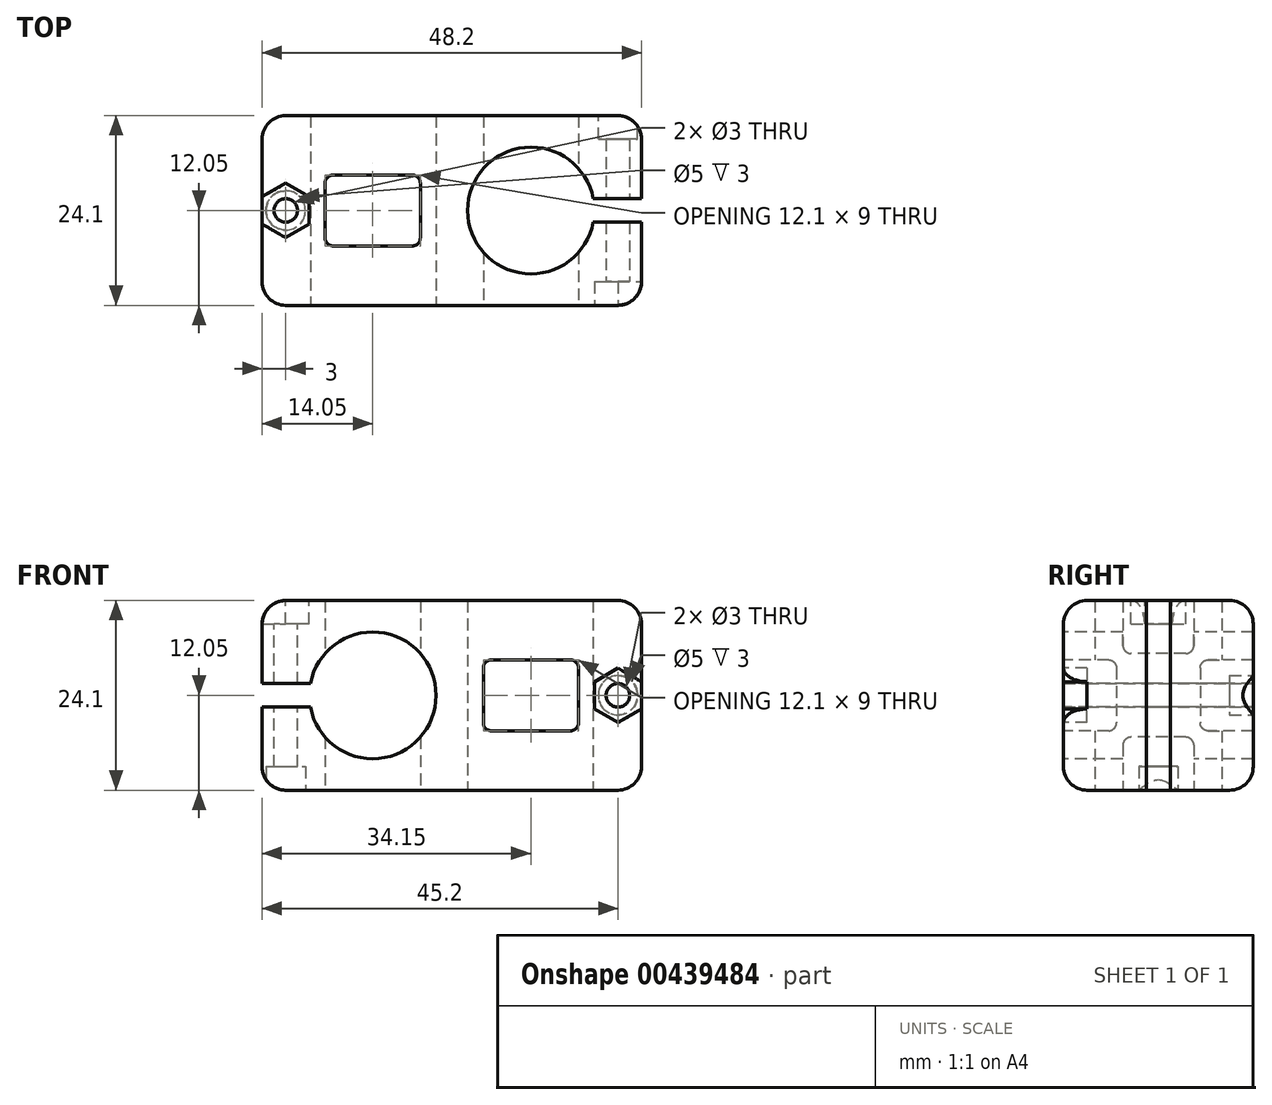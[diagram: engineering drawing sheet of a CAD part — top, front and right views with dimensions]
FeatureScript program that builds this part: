
annotation { "Feature Type Name" : "Feature", "Feature Type Description" : "" }
export const myFeature = defineFeature(function(context is Context, id is Id, definition is map)
    precondition{}
    {
        {
            var Q0;
            Q0=qCreatedBy(makeId("Top.planeOp"),FACE);
            var sketch = newSketch(context, id + "F0", { "sketchPlane" : qUnion([Q0])});
            skLineSegment(sketch, "E0", {"start": v(-10.05, 0) * mm, "end": v(10.05, 0) * mm, "construction": true});
            skCircle(sketch, "E1", {"center": v(10.05, 0) * mm, "radius": 8.05 * mm});
            skLineSegment(sketch, "E2.bottom", {"start": v(-24.1, 12.05) * mm, "end": v(24.1, 12.05) * mm});
            skLineSegment(sketch, "E2.top", {"start": v(-24.1, -12.05) * mm, "end": v(24.1, -12.05) * mm});
            skLineSegment(sketch, "E2.left", {"start": v(-24.1, 12.05) * mm, "end": v(-24.1, -12.05) * mm});
            skLineSegment(sketch, "E2.right", {"start": v(24.1, 12.05) * mm, "end": v(24.1, -12.05) * mm});
            skLineSegment(sketch, "E3.bottom", {"start": v(-16.1, 4.5) * mm, "end": v(-4, 4.5) * mm});
            skLineSegment(sketch, "E3.top", {"start": v(-16.1, -4.5) * mm, "end": v(-4, -4.5) * mm});
            skLineSegment(sketch, "E3.left", {"start": v(-16.1, 4.5) * mm, "end": v(-16.1, -4.5) * mm});
            skLineSegment(sketch, "E3.right", {"start": v(-4, 4.5) * mm, "end": v(-4, -4.5) * mm});
            skPoint(sketch, "E3.middle", {"position": v(-10.05, 0) * mm});
            skSolve(sketch);
        }
        {
            var Q0;
            Q0 = qSketchRegion(id + "F0", true);
            extrude(context, id + "F1", {"entities" : qUnion([Q0]), "endBound" : BoundingType.SYMMETRIC, "depth" : 24.1 * mm});
        }
        {
            var Q0;
            Q0=makeQuery(id+"F1.opExtrude","SWEPT_FACE",FACE,{"disambiguationData":[OSD([sQuery(id+"F0.wireOp",EDGE,"E2.top")])]});
            var sketch = newSketch(context, id + "F2", { "sketchPlane" : qUnion([Q0])});
            skLineSegment(sketch, "E4", {"start": v(10.05, 0) * mm, "end": v(-10.05, 0) * mm, "construction": true});
            skPoint(sketch, "E4.startSnap0", {"position": v(24.1, 0) * mm});
            skPoint(sketch, "E4.endSnap0", {"position": v(24.1, 0) * mm});
            skCircle(sketch, "E5", {"center": v(-10.05, 0) * mm, "radius": 8.05 * mm});
            skLineSegment(sketch, "E6.bottom", {"start": v(16.1, 4.5) * mm, "end": v(4, 4.5) * mm});
            skLineSegment(sketch, "E6.top", {"start": v(16.1, -4.5) * mm, "end": v(4, -4.5) * mm});
            skLineSegment(sketch, "E6.left", {"start": v(16.1, 4.5) * mm, "end": v(16.1, -4.5) * mm});
            skLineSegment(sketch, "E6.right", {"start": v(4, 4.5) * mm, "end": v(4, -4.5) * mm});
            skPoint(sketch, "E6.middle", {"position": v(10.05, 0) * mm});
            skSolve(sketch);
        }
        {
            var Q0;
            Q0 = qSketchRegion(id + "F2", true);
            extrude(context, id + "F3", {"entities" : qUnion([Q0]), "operationType" : NewBodyOperationType.REMOVE, "oppositeDirection" : true, "depth" : 25 * mm});
        }
        {
            var Q0;
            Q0=makeQuery(id+"F1.opExtrude","SWEPT_FACE",FACE,{"disambiguationData":[OSD([sQuery(id+"F0.wireOp",EDGE,"E2.bottom")])]});
            var sketch = newSketch(context, id + "F4", { "sketchPlane" : qUnion([Q0])});
            skLineSegment(sketch, "E7.bottom", {"start": v(16.26, -1.5) * mm, "end": v(36.47, -1.5) * mm});
            skLineSegment(sketch, "E7.top", {"start": v(16.26, 1.5) * mm, "end": v(36.47, 1.5) * mm});
            skLineSegment(sketch, "E7.left", {"start": v(16.26, -1.5) * mm, "end": v(16.26, 1.5) * mm});
            skLineSegment(sketch, "E7.right", {"start": v(36.47, -1.5) * mm, "end": v(36.47, 1.5) * mm});
            skPoint(sketch, "E7.middle", {"position": v(26.36, 0) * mm});
            skPoint(sketch, "E7.middle.positionSnap0", {"position": v(24.1, 0) * mm});
            skPoint(sketch, "E7.centerSnap0", {"position": v(24.1, 0) * mm});
            skSolve(sketch);
        }
        {
            var Q0;
            Q0 = qSketchRegion(id + "F4", true);
            extrude(context, id + "F5", {"entities" : qUnion([Q0]), "operationType" : NewBodyOperationType.REMOVE, "oppositeDirection" : true, "depth" : 25 * mm});
        }
        {
            var Q0;
            Q0=makeQuery(id+"F1.opExtrude","CAP_FACE",FACE,{"disambiguationData":[OSD([sQuery(id+"F0.wireOp",EDGE,"E1"),sQuery(id+"F0.wireOp",EDGE,"E2.bottom"),sQuery(id+"F0.wireOp",EDGE,"E2.top"),sQuery(id+"F0.wireOp",EDGE,"E2.left"),sQuery(id+"F0.wireOp",EDGE,"E2.right"),sQuery(id+"F0.wireOp",EDGE,"E3.bottom"),sQuery(id+"F0.wireOp",EDGE,"E3.top"),sQuery(id+"F0.wireOp",EDGE,"E3.left"),sQuery(id+"F0.wireOp",EDGE,"E3.right")])],"isStart":true});
            var sketch = newSketch(context, id + "F6", { "sketchPlane" : qUnion([Q0])});
            skLineSegment(sketch, "E8.bottom", {"start": v(16.57, 1.5) * mm, "end": v(31.63, 1.5) * mm});
            skLineSegment(sketch, "E8.top", {"start": v(16.57, -1.5) * mm, "end": v(31.63, -1.5) * mm});
            skLineSegment(sketch, "E8.left", {"start": v(16.57, 1.5) * mm, "end": v(16.57, -1.5) * mm});
            skLineSegment(sketch, "E8.right", {"start": v(31.63, 1.5) * mm, "end": v(31.63, -1.5) * mm});
            skPoint(sketch, "E8.middle", {"position": v(24.1, 0) * mm});
            skSolve(sketch);
        }
        {
            var Q0;
            Q0 = qSketchRegion(id + "F6", true);
            extrude(context, id + "F7", {"entities" : qUnion([Q0]), "operationType" : NewBodyOperationType.REMOVE, "endBound" : BoundingType.THROUGH_ALL, "oppositeDirection" : true, "depth" : 25 * mm});
        }
        {
            var Q0;
            Q0=makeQuery(id+"F1.opExtrude","SWEPT_FACE",FACE,{"disambiguationData":[OSD([sQuery(id+"F0.wireOp",EDGE,"E2.top")])]});
            var sketch = newSketch(context, id + "F8", { "sketchPlane" : qUnion([Q0])});
            skCircle(sketch, "E9.cCircle", {"center": v(21.1, 0) * mm, "radius": 3 * mm, "construction": true});
            skLineSegment(sketch, "E9.0", {"start": v(18.1, 1.73) * mm, "end": v(21.1, 3.46) * mm});
            skLineSegment(sketch, "E9.1", {"start": v(21.1, 3.46) * mm, "end": v(24.1, 1.73) * mm});
            skLineSegment(sketch, "E9.2", {"start": v(24.1, 1.73) * mm, "end": v(24.1, -1.73) * mm});
            skLineSegment(sketch, "E9.3", {"start": v(24.1, -1.73) * mm, "end": v(21.1, -3.46) * mm});
            skLineSegment(sketch, "E9.4", {"start": v(21.1, -3.46) * mm, "end": v(18.1, -1.73) * mm});
            skLineSegment(sketch, "E9.5", {"start": v(18.1, -1.73) * mm, "end": v(18.1, 1.73) * mm});
            skPoint(sketch, "E9.0.midPoint", {"position": v(19.6, 2.6) * mm});
            skSolve(sketch);
        }
        {
            var Q0;
            Q0 = qSketchRegion(id + "F8", true);
            extrude(context, id + "F9", {"entities" : qUnion([Q0]), "operationType" : NewBodyOperationType.REMOVE, "oppositeDirection" : true, "depth" : 3 * mm});
        }
        {
            var Q0;
            Q0=makeQuery(id+"F9.boolean.opBoolean","COPY",FACE,{"derivedFrom":makeQuery(id+"F9.opExtrude","CAP_FACE",FACE,{"disambiguationData":[OSD([sQuery(id+"F8.wireOp",EDGE,"E9.0"),sQuery(id+"F8.wireOp",EDGE,"E9.1"),sQuery(id+"F8.wireOp",EDGE,"E9.2"),sQuery(id+"F8.wireOp",EDGE,"E9.3"),sQuery(id+"F8.wireOp",EDGE,"E9.4"),sQuery(id+"F8.wireOp",EDGE,"E9.5")])],"isStart":false})});
            var sketch = newSketch(context, id + "F10", { "sketchPlane" : qUnion([Q0])});
            skLineSegment(sketch, "E10", {"start": v(21.1, 3.46) * mm, "end": v(21.1, -3.46) * mm, "construction": true});
            skCircle(sketch, "E11", {"center": v(21.1, 0) * mm, "radius": 1.5 * mm});
            skSolve(sketch);
        }
        {
            var Q0;
            Q0=makeQuery(id+"F10.imprint","IMPRINT",FACE,{"disambiguationData":[TD([[makeQuery(id+"F10.imprint","IMPRINT",EDGE,{"derivedFrom":sQuery(id+"F10.wireOp",EDGE,"E11")}),1.0]])]});
            extrude(context, id + "F11", {"entities" : qUnion([Q0]), "operationType" : NewBodyOperationType.REMOVE, "endBound" : BoundingType.THROUGH_ALL, "oppositeDirection" : true, "depth" : 25 * mm});
        }
        {
            var Q0;
            Q0=makeQuery(id+"F1.opExtrude","SWEPT_FACE",FACE,{"disambiguationData":[OSD([sQuery(id+"F0.wireOp",EDGE,"E2.bottom")])]});
            var sketch = newSketch(context, id + "F12", { "sketchPlane" : qUnion([Q0])});
            skCircle(sketch, "E12", {"center": v(-21.1, 0) * mm, "radius": 2.5 * mm});
            skSolve(sketch);
        }
        {
            var Q0;
            Q0 = qSketchRegion(id + "F12", true);
            extrude(context, id + "F13", {"entities" : qUnion([Q0]), "operationType" : NewBodyOperationType.REMOVE, "oppositeDirection" : true, "depth" : 3 * mm});
        }
        {
            var Q0;
            {var subQ0=sQuery(id+"F2.wireOp",EDGE,"E6.left");var subQ1=sQuery(id+"F2.wireOp",EDGE,"E6.bottom");Q0=makeQuery(id+"F3.boolean.opBoolean","COPY",EDGE,{"disambiguationData":[TD([makeQuery(id+"F1.opExtrude","SWEPT_FACE",FACE,{"disambiguationData":[OSD([sQuery(id+"F0.wireOp",EDGE,"E2.top")])]})])],"derivedFrom":makeQuery(id+"F3.opExtrude","SWEPT_EDGE",EDGE,{"disambiguationData":[OSD([subQ1,subQ0])]})});}
            var Q1;
            {var subQ0=sQuery(id+"F2.wireOp",EDGE,"E6.left");var subQ1=sQuery(id+"F2.wireOp",EDGE,"E6.top");Q1=makeQuery(id+"F3.boolean.opBoolean","COPY",EDGE,{"disambiguationData":[TD([makeQuery(id+"F1.opExtrude","SWEPT_FACE",FACE,{"disambiguationData":[OSD([sQuery(id+"F0.wireOp",EDGE,"E2.top")])]})])],"derivedFrom":makeQuery(id+"F3.opExtrude","SWEPT_EDGE",EDGE,{"disambiguationData":[OSD([subQ1,subQ0])]})});}
            var Q2;
            {var subQ0=sQuery(id+"F2.wireOp",EDGE,"E6.bottom");var subQ1=sQuery(id+"F2.wireOp",EDGE,"E6.right");Q2=makeQuery(id+"F3.boolean.opBoolean","COPY",EDGE,{"disambiguationData":[TD([makeQuery(id+"F1.opExtrude","SWEPT_FACE",FACE,{"disambiguationData":[OSD([sQuery(id+"F0.wireOp",EDGE,"E2.top")])]})])],"derivedFrom":makeQuery(id+"F3.opExtrude","SWEPT_EDGE",EDGE,{"disambiguationData":[OSD([subQ0,subQ1])]})});}
            var Q3;
            {var subQ0=sQuery(id+"F2.wireOp",EDGE,"E6.top");var subQ1=sQuery(id+"F2.wireOp",EDGE,"E6.right");Q3=makeQuery(id+"F3.boolean.opBoolean","COPY",EDGE,{"disambiguationData":[TD([makeQuery(id+"F1.opExtrude","SWEPT_FACE",FACE,{"disambiguationData":[OSD([sQuery(id+"F0.wireOp",EDGE,"E2.top")])]})])],"derivedFrom":makeQuery(id+"F3.opExtrude","SWEPT_EDGE",EDGE,{"disambiguationData":[OSD([subQ0,subQ1])]})});}
            var Q4;
            {var subQ0=sQuery(id+"F0.wireOp",EDGE,"E3.right");var subQ1=sQuery(id+"F0.wireOp",EDGE,"E3.top");Q4=makeQuery(id+"F3.boolean.opBoolean","SPLIT",EDGE,{"disambiguationData":[TD([makeQuery(id+"F1.opExtrude","CAP_FACE",FACE,{"disambiguationData":[OSD([sQuery(id+"F0.wireOp",EDGE,"E1"),sQuery(id+"F0.wireOp",EDGE,"E2.bottom"),sQuery(id+"F0.wireOp",EDGE,"E2.top"),sQuery(id+"F0.wireOp",EDGE,"E2.left"),sQuery(id+"F0.wireOp",EDGE,"E2.right"),sQuery(id+"F0.wireOp",EDGE,"E3.bottom"),subQ1,sQuery(id+"F0.wireOp",EDGE,"E3.left"),subQ0])],"isStart":false})])],"derivedFrom":makeQuery(id+"F1.opExtrude","SWEPT_EDGE",EDGE,{"disambiguationData":[OSD([subQ1,subQ0])]})});}
            var Q5;
            {var subQ0=sQuery(id+"F0.wireOp",EDGE,"E3.right");var subQ1=sQuery(id+"F0.wireOp",EDGE,"E3.bottom");Q5=makeQuery(id+"F3.boolean.opBoolean","SPLIT",EDGE,{"disambiguationData":[TD([makeQuery(id+"F1.opExtrude","CAP_FACE",FACE,{"disambiguationData":[OSD([sQuery(id+"F0.wireOp",EDGE,"E1"),sQuery(id+"F0.wireOp",EDGE,"E2.bottom"),sQuery(id+"F0.wireOp",EDGE,"E2.top"),sQuery(id+"F0.wireOp",EDGE,"E2.left"),sQuery(id+"F0.wireOp",EDGE,"E2.right"),subQ1,sQuery(id+"F0.wireOp",EDGE,"E3.top"),sQuery(id+"F0.wireOp",EDGE,"E3.left"),subQ0])],"isStart":false})])],"derivedFrom":makeQuery(id+"F1.opExtrude","SWEPT_EDGE",EDGE,{"disambiguationData":[OSD([subQ1,subQ0])]})});}
            var Q6;
            {var subQ0=sQuery(id+"F0.wireOp",EDGE,"E3.left");var subQ1=sQuery(id+"F0.wireOp",EDGE,"E3.top");Q6=makeQuery(id+"F3.boolean.opBoolean","SPLIT",EDGE,{"disambiguationData":[TD([makeQuery(id+"F1.opExtrude","CAP_FACE",FACE,{"disambiguationData":[OSD([sQuery(id+"F0.wireOp",EDGE,"E1"),sQuery(id+"F0.wireOp",EDGE,"E2.bottom"),sQuery(id+"F0.wireOp",EDGE,"E2.top"),sQuery(id+"F0.wireOp",EDGE,"E2.left"),sQuery(id+"F0.wireOp",EDGE,"E2.right"),sQuery(id+"F0.wireOp",EDGE,"E3.bottom"),subQ1,subQ0,sQuery(id+"F0.wireOp",EDGE,"E3.right")])],"isStart":false})])],"derivedFrom":makeQuery(id+"F1.opExtrude","SWEPT_EDGE",EDGE,{"disambiguationData":[OSD([subQ1,subQ0])]})});}
            var Q7;
            {var subQ0=sQuery(id+"F0.wireOp",EDGE,"E3.left");var subQ1=sQuery(id+"F0.wireOp",EDGE,"E3.bottom");Q7=makeQuery(id+"F3.boolean.opBoolean","SPLIT",EDGE,{"disambiguationData":[TD([makeQuery(id+"F1.opExtrude","CAP_FACE",FACE,{"disambiguationData":[OSD([sQuery(id+"F0.wireOp",EDGE,"E1"),sQuery(id+"F0.wireOp",EDGE,"E2.bottom"),sQuery(id+"F0.wireOp",EDGE,"E2.top"),sQuery(id+"F0.wireOp",EDGE,"E2.left"),sQuery(id+"F0.wireOp",EDGE,"E2.right"),subQ1,sQuery(id+"F0.wireOp",EDGE,"E3.top"),subQ0,sQuery(id+"F0.wireOp",EDGE,"E3.right")])],"isStart":false})])],"derivedFrom":makeQuery(id+"F1.opExtrude","SWEPT_EDGE",EDGE,{"disambiguationData":[OSD([subQ1,subQ0])]})});}
            var Q8;
            {var subQ0=sQuery(id+"F0.wireOp",EDGE,"E3.right");var subQ1=sQuery(id+"F0.wireOp",EDGE,"E3.bottom");Q8=makeQuery(id+"F3.boolean.opBoolean","SPLIT",EDGE,{"disambiguationData":[TD([makeQuery(id+"F1.opExtrude","CAP_FACE",FACE,{"disambiguationData":[OSD([sQuery(id+"F0.wireOp",EDGE,"E1"),sQuery(id+"F0.wireOp",EDGE,"E2.bottom"),sQuery(id+"F0.wireOp",EDGE,"E2.top"),sQuery(id+"F0.wireOp",EDGE,"E2.left"),sQuery(id+"F0.wireOp",EDGE,"E2.right"),subQ1,sQuery(id+"F0.wireOp",EDGE,"E3.top"),sQuery(id+"F0.wireOp",EDGE,"E3.left"),subQ0])],"isStart":true})])],"derivedFrom":makeQuery(id+"F1.opExtrude","SWEPT_EDGE",EDGE,{"disambiguationData":[OSD([subQ1,subQ0])]})});}
            var Q9;
            {var subQ0=sQuery(id+"F0.wireOp",EDGE,"E3.left");var subQ1=sQuery(id+"F0.wireOp",EDGE,"E3.bottom");Q9=makeQuery(id+"F3.boolean.opBoolean","SPLIT",EDGE,{"disambiguationData":[TD([makeQuery(id+"F1.opExtrude","CAP_FACE",FACE,{"disambiguationData":[OSD([sQuery(id+"F0.wireOp",EDGE,"E1"),sQuery(id+"F0.wireOp",EDGE,"E2.bottom"),sQuery(id+"F0.wireOp",EDGE,"E2.top"),sQuery(id+"F0.wireOp",EDGE,"E2.left"),sQuery(id+"F0.wireOp",EDGE,"E2.right"),subQ1,sQuery(id+"F0.wireOp",EDGE,"E3.top"),subQ0,sQuery(id+"F0.wireOp",EDGE,"E3.right")])],"isStart":true})])],"derivedFrom":makeQuery(id+"F1.opExtrude","SWEPT_EDGE",EDGE,{"disambiguationData":[OSD([subQ1,subQ0])]})});}
            var Q10;
            {var subQ0=sQuery(id+"F0.wireOp",EDGE,"E3.left");var subQ1=sQuery(id+"F0.wireOp",EDGE,"E3.top");Q10=makeQuery(id+"F3.boolean.opBoolean","SPLIT",EDGE,{"disambiguationData":[TD([makeQuery(id+"F1.opExtrude","CAP_FACE",FACE,{"disambiguationData":[OSD([sQuery(id+"F0.wireOp",EDGE,"E1"),sQuery(id+"F0.wireOp",EDGE,"E2.bottom"),sQuery(id+"F0.wireOp",EDGE,"E2.top"),sQuery(id+"F0.wireOp",EDGE,"E2.left"),sQuery(id+"F0.wireOp",EDGE,"E2.right"),sQuery(id+"F0.wireOp",EDGE,"E3.bottom"),subQ1,subQ0,sQuery(id+"F0.wireOp",EDGE,"E3.right")])],"isStart":true})])],"derivedFrom":makeQuery(id+"F1.opExtrude","SWEPT_EDGE",EDGE,{"disambiguationData":[OSD([subQ1,subQ0])]})});}
            var Q11;
            {var subQ0=sQuery(id+"F0.wireOp",EDGE,"E3.right");var subQ1=sQuery(id+"F0.wireOp",EDGE,"E3.top");Q11=makeQuery(id+"F3.boolean.opBoolean","SPLIT",EDGE,{"disambiguationData":[TD([makeQuery(id+"F1.opExtrude","CAP_FACE",FACE,{"disambiguationData":[OSD([sQuery(id+"F0.wireOp",EDGE,"E1"),sQuery(id+"F0.wireOp",EDGE,"E2.bottom"),sQuery(id+"F0.wireOp",EDGE,"E2.top"),sQuery(id+"F0.wireOp",EDGE,"E2.left"),sQuery(id+"F0.wireOp",EDGE,"E2.right"),sQuery(id+"F0.wireOp",EDGE,"E3.bottom"),subQ1,sQuery(id+"F0.wireOp",EDGE,"E3.left"),subQ0])],"isStart":true})])],"derivedFrom":makeQuery(id+"F1.opExtrude","SWEPT_EDGE",EDGE,{"disambiguationData":[OSD([subQ1,subQ0])]})});}
            var Q12;
            {var subQ0=sQuery(id+"F2.wireOp",EDGE,"E6.bottom");var subQ1=sQuery(id+"F2.wireOp",EDGE,"E6.right");Q12=makeQuery(id+"F3.boolean.opBoolean","COPY",EDGE,{"disambiguationData":[TD([makeQuery(id+"F1.opExtrude","SWEPT_FACE",FACE,{"disambiguationData":[OSD([sQuery(id+"F0.wireOp",EDGE,"E2.bottom")])]})])],"derivedFrom":makeQuery(id+"F3.opExtrude","SWEPT_EDGE",EDGE,{"disambiguationData":[OSD([subQ0,subQ1])]})});}
            var Q13;
            {var subQ0=sQuery(id+"F2.wireOp",EDGE,"E6.left");var subQ1=sQuery(id+"F2.wireOp",EDGE,"E6.bottom");Q13=makeQuery(id+"F3.boolean.opBoolean","COPY",EDGE,{"disambiguationData":[TD([makeQuery(id+"F1.opExtrude","SWEPT_FACE",FACE,{"disambiguationData":[OSD([sQuery(id+"F0.wireOp",EDGE,"E2.bottom")])]})])],"derivedFrom":makeQuery(id+"F3.opExtrude","SWEPT_EDGE",EDGE,{"disambiguationData":[OSD([subQ1,subQ0])]})});}
            var Q14;
            {var subQ0=sQuery(id+"F2.wireOp",EDGE,"E6.left");var subQ1=sQuery(id+"F2.wireOp",EDGE,"E6.top");Q14=makeQuery(id+"F3.boolean.opBoolean","COPY",EDGE,{"disambiguationData":[TD([makeQuery(id+"F1.opExtrude","SWEPT_FACE",FACE,{"disambiguationData":[OSD([sQuery(id+"F0.wireOp",EDGE,"E2.bottom")])]})])],"derivedFrom":makeQuery(id+"F3.opExtrude","SWEPT_EDGE",EDGE,{"disambiguationData":[OSD([subQ1,subQ0])]})});}
            var Q15;
            {var subQ0=sQuery(id+"F2.wireOp",EDGE,"E6.top");var subQ1=sQuery(id+"F2.wireOp",EDGE,"E6.right");Q15=makeQuery(id+"F3.boolean.opBoolean","COPY",EDGE,{"disambiguationData":[TD([makeQuery(id+"F1.opExtrude","SWEPT_FACE",FACE,{"disambiguationData":[OSD([sQuery(id+"F0.wireOp",EDGE,"E2.bottom")])]})])],"derivedFrom":makeQuery(id+"F3.opExtrude","SWEPT_EDGE",EDGE,{"disambiguationData":[OSD([subQ0,subQ1])]})});}
            fillet(context, id + "F14", {"entities" : qUnion([Q0, Q1, Q2, Q3, Q4, Q5, Q6, Q7, Q8, Q9, Q10, Q11, Q12, Q13, Q14, Q15]), "radius" : 1 * mm, "tangentPropagation" : true, "allowEdgeOverflow" : false});
        }
        {
            var Q0;
            Q0=makeQuery(id+"F1.opExtrude","CAP_FACE",FACE,{"disambiguationData":[OSD([sQuery(id+"F0.wireOp",EDGE,"E1"),sQuery(id+"F0.wireOp",EDGE,"E2.bottom"),sQuery(id+"F0.wireOp",EDGE,"E2.top"),sQuery(id+"F0.wireOp",EDGE,"E2.left"),sQuery(id+"F0.wireOp",EDGE,"E2.right"),sQuery(id+"F0.wireOp",EDGE,"E3.bottom"),sQuery(id+"F0.wireOp",EDGE,"E3.top"),sQuery(id+"F0.wireOp",EDGE,"E3.left"),sQuery(id+"F0.wireOp",EDGE,"E3.right")])],"isStart":false});
            var sketch = newSketch(context, id + "F15", { "sketchPlane" : qUnion([Q0])});
            skCircle(sketch, "E13.cCircle", {"center": v(-21.1, 0) * mm, "radius": 3 * mm, "construction": true});
            skLineSegment(sketch, "E13.0", {"start": v(-24.1, 1.73) * mm, "end": v(-21.1, 3.46) * mm});
            skLineSegment(sketch, "E13.1", {"start": v(-21.1, 3.46) * mm, "end": v(-18.1, 1.73) * mm});
            skLineSegment(sketch, "E13.2", {"start": v(-18.1, 1.73) * mm, "end": v(-18.1, -1.73) * mm});
            skLineSegment(sketch, "E13.3", {"start": v(-18.1, -1.73) * mm, "end": v(-21.1, -3.46) * mm});
            skLineSegment(sketch, "E13.4", {"start": v(-21.1, -3.46) * mm, "end": v(-24.1, -1.73) * mm});
            skLineSegment(sketch, "E13.5", {"start": v(-24.1, -1.73) * mm, "end": v(-24.1, 1.73) * mm});
            skPoint(sketch, "E13.0.midPoint", {"position": v(-22.6, 2.6) * mm});
            skSolve(sketch);
        }
        {
            var Q0;
            Q0 = qSketchRegion(id + "F15", true);
            extrude(context, id + "F16", {"entities" : qUnion([Q0]), "operationType" : NewBodyOperationType.REMOVE, "oppositeDirection" : true, "depth" : 3 * mm});
        }
        {
            var Q0;
            Q0=makeQuery(id+"F16.boolean.opBoolean","COPY",FACE,{"derivedFrom":makeQuery(id+"F16.opExtrude","CAP_FACE",FACE,{"disambiguationData":[OSD([sQuery(id+"F15.wireOp",EDGE,"E13.0"),sQuery(id+"F15.wireOp",EDGE,"E13.1"),sQuery(id+"F15.wireOp",EDGE,"E13.2"),sQuery(id+"F15.wireOp",EDGE,"E13.3"),sQuery(id+"F15.wireOp",EDGE,"E13.4"),sQuery(id+"F15.wireOp",EDGE,"E13.5")])],"isStart":false})});
            var sketch = newSketch(context, id + "F17", { "sketchPlane" : qUnion([Q0])});
            skLineSegment(sketch, "E14", {"start": v(-21.1, 3.46) * mm, "end": v(-21.1, -3.46) * mm, "construction": true});
            skCircle(sketch, "E15", {"center": v(-21.1, 0) * mm, "radius": 1.5 * mm});
            skSolve(sketch);
        }
        {
            var Q0;
            Q0 = qSketchRegion(id + "F17", true);
            extrude(context, id + "F18", {"entities" : qUnion([Q0]), "operationType" : NewBodyOperationType.REMOVE, "endBound" : BoundingType.THROUGH_ALL, "oppositeDirection" : true, "depth" : 25 * mm});
        }
        {
            var Q0;
            Q0=makeQuery(id+"F1.opExtrude","CAP_FACE",FACE,{"disambiguationData":[OSD([sQuery(id+"F0.wireOp",EDGE,"E1"),sQuery(id+"F0.wireOp",EDGE,"E2.bottom"),sQuery(id+"F0.wireOp",EDGE,"E2.top"),sQuery(id+"F0.wireOp",EDGE,"E2.left"),sQuery(id+"F0.wireOp",EDGE,"E2.right"),sQuery(id+"F0.wireOp",EDGE,"E3.bottom"),sQuery(id+"F0.wireOp",EDGE,"E3.top"),sQuery(id+"F0.wireOp",EDGE,"E3.left"),sQuery(id+"F0.wireOp",EDGE,"E3.right")])],"isStart":true});
            var sketch = newSketch(context, id + "F19", { "sketchPlane" : qUnion([Q0])});
            skCircle(sketch, "E16", {"center": v(-21.1, 0) * mm, "radius": 2.5 * mm});
            skSolve(sketch);
        }
        {
            var Q0;
            Q0 = qSketchRegion(id + "F19", true);
            extrude(context, id + "F20", {"entities" : qUnion([Q0]), "operationType" : NewBodyOperationType.REMOVE, "oppositeDirection" : true, "depth" : 3 * mm});
        }
        {
            var Q0;
            Q0=makeQuery(id+"F1.opExtrude","CAP_EDGE",EDGE,{"disambiguationData":[OSD([sQuery(id+"F0.wireOp",EDGE,"E2.left")])],"isStart":true});
            var Q1;
            Q1=makeQuery(id+"F1.opExtrude","CAP_EDGE",EDGE,{"disambiguationData":[OSD([sQuery(id+"F0.wireOp",EDGE,"E2.top")])],"isStart":true});
            var Q2;
            Q2=makeQuery(id+"F1.opExtrude","CAP_EDGE",EDGE,{"disambiguationData":[OSD([sQuery(id+"F0.wireOp",EDGE,"E2.bottom")])],"isStart":true});
            var Q3;
            {var subQ0=sQuery(id+"F0.wireOp",EDGE,"E2.right");var subQ1=sQuery(id+"F0.wireOp",EDGE,"E2.bottom");Q3=makeQuery(id+"F7.boolean.opBoolean","SPLIT",EDGE,{"disambiguationData":[TD([makeQuery(id+"F1.opExtrude","SWEPT_FACE",FACE,{"disambiguationData":[OSD([subQ1])]})])],"derivedFrom":makeQuery(id+"F1.opExtrude","CAP_EDGE",EDGE,{"disambiguationData":[OSD([subQ0])],"isStart":true})});}
            var Q4;
            {var subQ0=sQuery(id+"F0.wireOp",EDGE,"E2.right");var subQ1=sQuery(id+"F0.wireOp",EDGE,"E2.top");Q4=makeQuery(id+"F7.boolean.opBoolean","SPLIT",EDGE,{"disambiguationData":[TD([makeQuery(id+"F1.opExtrude","SWEPT_FACE",FACE,{"disambiguationData":[OSD([subQ1])]})])],"derivedFrom":makeQuery(id+"F1.opExtrude","CAP_EDGE",EDGE,{"disambiguationData":[OSD([subQ0])],"isStart":true})});}
            var Q5;
            {var subQ0=sQuery(id+"F0.wireOp",EDGE,"E2.right");var subQ1=sQuery(id+"F0.wireOp",EDGE,"E2.top");Q5=makeQuery(id+"F9.boolean.opBoolean","SPLIT",EDGE,{"disambiguationData":[TD([makeQuery(id+"F9.opExtrude","SWEPT_FACE",FACE,{"disambiguationData":[OSD([sQuery(id+"F8.wireOp",EDGE,"E9.3")])]})])],"derivedFrom":makeQuery(id+"F1.opExtrude","SWEPT_EDGE",EDGE,{"disambiguationData":[OSD([subQ1,subQ0])]})});}
            var Q6;
            {var subQ0=sQuery(id+"F0.wireOp",EDGE,"E2.right");var subQ1=sQuery(id+"F0.wireOp",EDGE,"E2.top");Q6=makeQuery(id+"F9.boolean.opBoolean","SPLIT",EDGE,{"disambiguationData":[TD([makeQuery(id+"F9.opExtrude","SWEPT_FACE",FACE,{"disambiguationData":[OSD([sQuery(id+"F8.wireOp",EDGE,"E9.1")])]})])],"derivedFrom":makeQuery(id+"F1.opExtrude","SWEPT_EDGE",EDGE,{"disambiguationData":[OSD([subQ1,subQ0])]})});}
            var Q7;
            Q7=makeQuery(id+"F1.opExtrude","SWEPT_EDGE",EDGE,{"disambiguationData":[OSD([sQuery(id+"F0.wireOp",EDGE,"E2.bottom"),sQuery(id+"F0.wireOp",EDGE,"E2.right")])]});
            var Q8;
            {var subQ0=sQuery(id+"F0.wireOp",EDGE,"E2.right");var subQ1=sQuery(id+"F0.wireOp",EDGE,"E2.bottom");Q8=makeQuery(id+"F7.boolean.opBoolean","SPLIT",EDGE,{"disambiguationData":[TD([makeQuery(id+"F1.opExtrude","SWEPT_FACE",FACE,{"disambiguationData":[OSD([subQ1])]})])],"derivedFrom":makeQuery(id+"F1.opExtrude","CAP_EDGE",EDGE,{"disambiguationData":[OSD([subQ0])],"isStart":false})});}
            var Q9;
            {var subQ0=sQuery(id+"F0.wireOp",EDGE,"E2.right");var subQ1=sQuery(id+"F0.wireOp",EDGE,"E2.top");Q9=makeQuery(id+"F7.boolean.opBoolean","SPLIT",EDGE,{"disambiguationData":[TD([makeQuery(id+"F1.opExtrude","SWEPT_FACE",FACE,{"disambiguationData":[OSD([subQ1])]})])],"derivedFrom":makeQuery(id+"F1.opExtrude","CAP_EDGE",EDGE,{"disambiguationData":[OSD([subQ0])],"isStart":false})});}
            var Q10;
            Q10=makeQuery(id+"F1.opExtrude","CAP_EDGE",EDGE,{"disambiguationData":[OSD([sQuery(id+"F0.wireOp",EDGE,"E2.bottom")])],"isStart":false});
            var Q11;
            Q11=makeQuery(id+"F1.opExtrude","CAP_EDGE",EDGE,{"disambiguationData":[OSD([sQuery(id+"F0.wireOp",EDGE,"E2.top")])],"isStart":false});
            var Q12;
            {var subQ0=sQuery(id+"F0.wireOp",EDGE,"E2.left");var subQ1=sQuery(id+"F0.wireOp",EDGE,"E2.top");Q12=makeQuery(id+"F16.boolean.opBoolean","SPLIT",EDGE,{"disambiguationData":[TD([makeQuery(id+"F1.opExtrude","SWEPT_FACE",FACE,{"disambiguationData":[OSD([subQ1])]})])],"derivedFrom":makeQuery(id+"F1.opExtrude","CAP_EDGE",EDGE,{"disambiguationData":[OSD([subQ0])],"isStart":false})});}
            var Q13;
            {var subQ0=sQuery(id+"F0.wireOp",EDGE,"E2.left");var subQ1=sQuery(id+"F0.wireOp",EDGE,"E2.bottom");Q13=makeQuery(id+"F16.boolean.opBoolean","SPLIT",EDGE,{"disambiguationData":[TD([makeQuery(id+"F1.opExtrude","SWEPT_FACE",FACE,{"disambiguationData":[OSD([subQ1])]})])],"derivedFrom":makeQuery(id+"F1.opExtrude","CAP_EDGE",EDGE,{"disambiguationData":[OSD([subQ0])],"isStart":false})});}
            var Q14;
            {var subQ0=sQuery(id+"F0.wireOp",EDGE,"E2.left");var subQ1=sQuery(id+"F0.wireOp",EDGE,"E2.top");Q14=makeQuery(id+"F5.boolean.opBoolean","SPLIT",EDGE,{"disambiguationData":[TD([makeQuery(id+"F5.opExtrude","SWEPT_FACE",FACE,{"disambiguationData":[OSD([sQuery(id+"F4.wireOp",EDGE,"E7.top")])]})])],"derivedFrom":makeQuery(id+"F1.opExtrude","SWEPT_EDGE",EDGE,{"disambiguationData":[OSD([subQ1,subQ0])]})});}
            var Q15;
            {var subQ0=sQuery(id+"F0.wireOp",EDGE,"E2.left");var subQ1=sQuery(id+"F0.wireOp",EDGE,"E2.top");Q15=makeQuery(id+"F5.boolean.opBoolean","SPLIT",EDGE,{"disambiguationData":[TD([makeQuery(id+"F5.opExtrude","SWEPT_FACE",FACE,{"disambiguationData":[OSD([sQuery(id+"F4.wireOp",EDGE,"E7.bottom")])]})])],"derivedFrom":makeQuery(id+"F1.opExtrude","SWEPT_EDGE",EDGE,{"disambiguationData":[OSD([subQ1,subQ0])]})});}
            var Q16;
            {var subQ0=sQuery(id+"F0.wireOp",EDGE,"E2.left");var subQ1=sQuery(id+"F0.wireOp",EDGE,"E2.bottom");Q16=makeQuery(id+"F5.boolean.opBoolean","SPLIT",EDGE,{"disambiguationData":[TD([makeQuery(id+"F5.opExtrude","SWEPT_FACE",FACE,{"disambiguationData":[OSD([sQuery(id+"F4.wireOp",EDGE,"E7.bottom")])]})])],"derivedFrom":makeQuery(id+"F1.opExtrude","SWEPT_EDGE",EDGE,{"disambiguationData":[OSD([subQ1,subQ0])]})});}
            var Q17;
            {var subQ0=sQuery(id+"F0.wireOp",EDGE,"E2.left");var subQ1=sQuery(id+"F0.wireOp",EDGE,"E2.bottom");Q17=makeQuery(id+"F5.boolean.opBoolean","SPLIT",EDGE,{"disambiguationData":[TD([makeQuery(id+"F5.opExtrude","SWEPT_FACE",FACE,{"disambiguationData":[OSD([sQuery(id+"F4.wireOp",EDGE,"E7.top")])]})])],"derivedFrom":makeQuery(id+"F1.opExtrude","SWEPT_EDGE",EDGE,{"disambiguationData":[OSD([subQ1,subQ0])]})});}
            fillet(context, id + "F21", {"entities" : qUnion([Q0, Q1, Q2, Q3, Q4, Q5, Q6, Q7, Q8, Q9, Q10, Q11, Q12, Q13, Q14, Q15, Q16, Q17]), "radius" : 3 * mm, "tangentPropagation" : true, "allowEdgeOverflow" : false});
        }
    });
